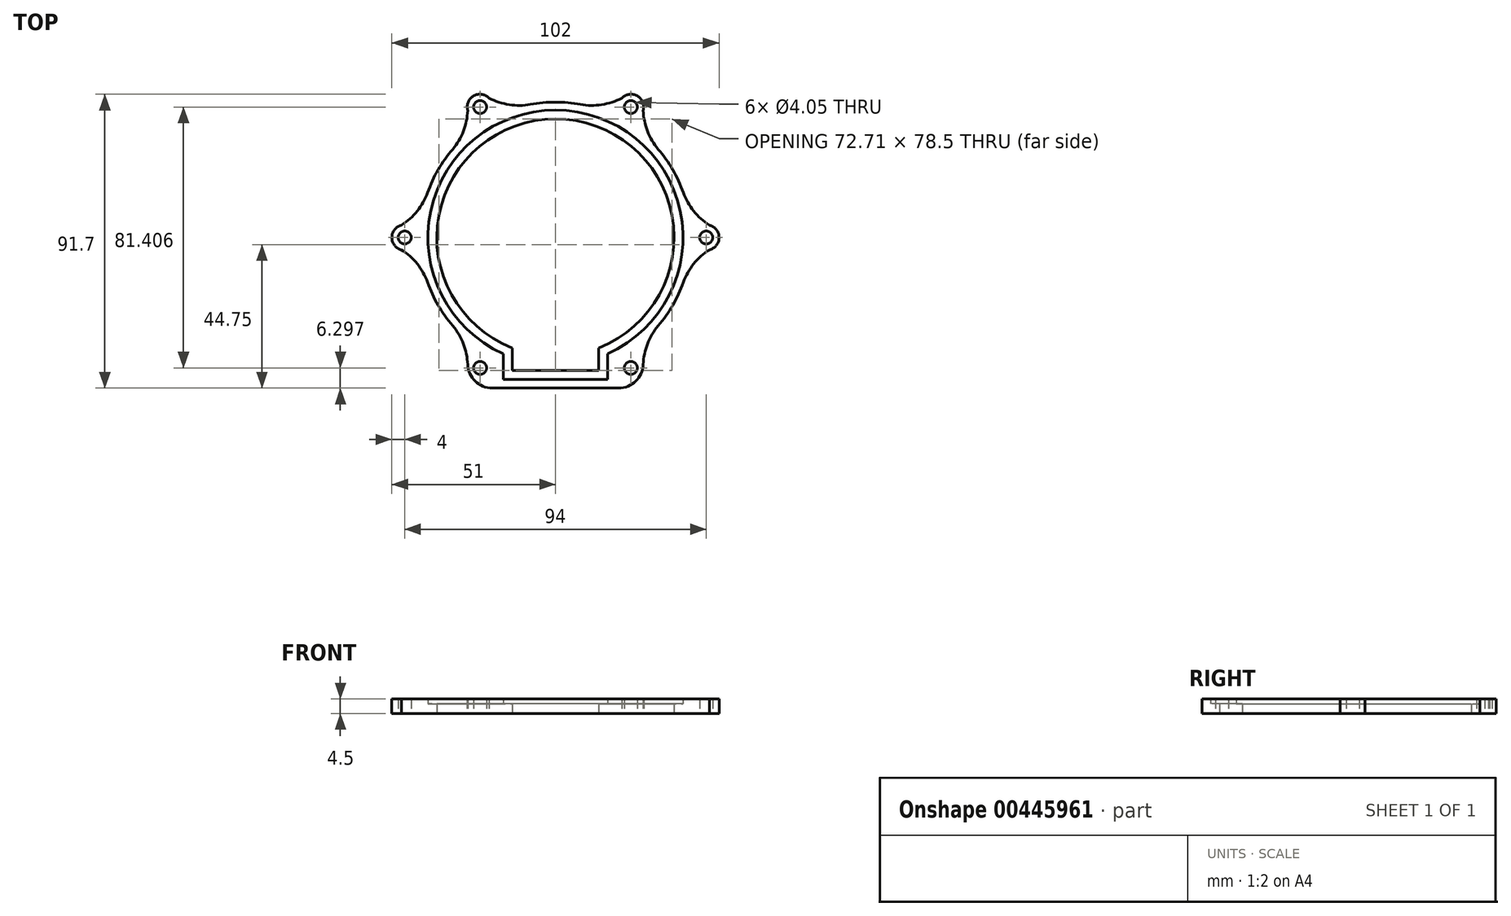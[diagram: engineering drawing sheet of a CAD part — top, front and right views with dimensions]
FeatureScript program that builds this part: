
annotation { "Feature Type Name" : "Feature", "Feature Type Description" : "" }
export const myFeature = defineFeature(function(context is Context, id is Id, definition is map)
    precondition{}
    {
        {
            var Q0;
            Q0=qCreatedBy(makeId("Top.planeOp"),FACE);
            var sketch = newSketch(context, id + "F0", { "sketchPlane" : qUnion([Q0])});
            skArc(sketch, "E0", {"start": v(13.5, -34.45) * mm, "mid": v(0, 37) * mm, "end": v(-13.5, -34.45) * mm});
            skArc(sketch, "E1", {"start": v(16.25, -36.28) * mm, "mid": v(0, 39.75) * mm, "end": v(-16.25, -36.28) * mm});
            skArc(sketch, "E2", {"start": v(-32.06, 27.52) * mm, "mid": v(-36.59, 21.12) * mm, "end": v(-39.86, 14) * mm});
            skArc(sketch, "E3", {"start": v(-48, 3.87) * mm, "mid": v(-51, 0) * mm, "end": v(-48, -3.87) * mm});
            skCircle(sketch, "E4", {"center": v(-47, 0) * mm, "radius": 2.02 * mm});
            skArc(sketch, "E5", {"start": v(-48, 3.87) * mm, "mid": v(-43.09, 8.26) * mm, "end": v(-39.86, 14) * mm});
            skArc(sketch, "E6.MirrorCS", {"start": v(-48, -3.87) * mm, "mid": v(-43.09, -8.26) * mm, "end": v(-39.86, -14) * mm});
            skArc(sketch, "E7.1.0", {"start": v(-27.35, -39.63) * mm, "mid": v(-28.7, -33.19) * mm, "end": v(-32.06, -27.52) * mm});
            skCircle(sketch, "E7.1.2", {"center": v(-23.5, -40.7) * mm, "radius": 2.02 * mm});
            skCircle(sketch, "E7.2.2", {"center": v(23.5, -40.7) * mm, "radius": 2.02 * mm});
            skArc(sketch, "E7.2.3", {"start": v(27.35, -39.63) * mm, "mid": v(28.7, -33.19) * mm, "end": v(32.06, -27.52) * mm});
            skArc(sketch, "E7.3.0", {"start": v(48, -3.87) * mm, "mid": v(43.09, -8.26) * mm, "end": v(39.86, -14) * mm});
            skArc(sketch, "E7.3.1", {"start": v(48, -3.87) * mm, "mid": v(51, 0) * mm, "end": v(48, 3.87) * mm});
            skCircle(sketch, "E7.3.2", {"center": v(47, 0) * mm, "radius": 2.02 * mm});
            skArc(sketch, "E7.3.3", {"start": v(48, 3.87) * mm, "mid": v(43.09, 8.26) * mm, "end": v(39.86, 14) * mm});
            skArc(sketch, "E7.4.0", {"start": v(27.35, 39.63) * mm, "mid": v(28.7, 33.19) * mm, "end": v(32.06, 27.52) * mm});
            skArc(sketch, "E7.4.1", {"start": v(27.35, 39.63) * mm, "mid": v(25.5, 44.17) * mm, "end": v(20.65, 43.5) * mm});
            skCircle(sketch, "E7.4.2", {"center": v(23.5, 40.7) * mm, "radius": 2.02 * mm});
            skArc(sketch, "E7.4.3", {"start": v(20.65, 43.5) * mm, "mid": v(14.4, 41.44) * mm, "end": v(7.8, 41.52) * mm});
            skArc(sketch, "E7.5.0", {"start": v(-20.65, 43.5) * mm, "mid": v(-14.4, 41.44) * mm, "end": v(-7.8, 41.52) * mm});
            skArc(sketch, "E7.5.1", {"start": v(-20.65, 43.5) * mm, "mid": v(-25.5, 44.17) * mm, "end": v(-27.35, 39.63) * mm});
            skCircle(sketch, "E7.5.2", {"center": v(-23.5, 40.7) * mm, "radius": 2.02 * mm});
            skArc(sketch, "E7.5.3", {"start": v(-27.35, 39.63) * mm, "mid": v(-28.7, 33.19) * mm, "end": v(-32.06, 27.52) * mm});
            skArc(sketch, "E8.trimOffspring", {"start": v(7.8, 41.52) * mm, "mid": v(0, 42.25) * mm, "end": v(-7.8, 41.52) * mm});
            skArc(sketch, "E9.trimOffspring", {"start": v(39.86, 14) * mm, "mid": v(36.59, 21.12) * mm, "end": v(32.06, 27.52) * mm});
            skArc(sketch, "E10.trimOffspring", {"start": v(32.06, -27.52) * mm, "mid": v(36.59, -21.13) * mm, "end": v(39.86, -14) * mm});
            skArc(sketch, "E11.trimOffspring", {"start": v(-39.86, -14) * mm, "mid": v(-36.59, -21.12) * mm, "end": v(-32.06, -27.52) * mm});
            skLineSegment(sketch, "E12.top", {"start": v(16.25, -44.25) * mm, "end": v(-16.25, -44.25) * mm});
            skLineSegment(sketch, "E12.left", {"start": v(16.25, -33.18) * mm, "end": v(16.25, -33.24) * mm});
            skLineSegment(sketch, "E12.right", {"start": v(-16.25, -33.18) * mm, "end": v(-16.25, -33.24) * mm});
            skPoint(sketch, "E12.middle", {"position": v(0, -38.72) * mm});
            skLineSegment(sketch, "E13.0", {"start": v(-13.5, -34.45) * mm, "end": v(-13.5, -41.5) * mm});
            skLineSegment(sketch, "E13.1", {"start": v(13.5, -41.5) * mm, "end": v(-13.5, -41.5) * mm});
            skLineSegment(sketch, "E13.2", {"start": v(13.5, -34.45) * mm, "end": v(13.5, -41.5) * mm});
            skLineSegment(sketch, "E14.1", {"start": v(19.69, -47) * mm, "end": v(-19.69, -47) * mm});
            skArc(sketch, "E15.trimOffspring", {"start": v(7.93, -41.5) * mm, "mid": v(7.87, -41.51) * mm, "end": v(7.8, -41.52) * mm});
            skArc(sketch, "E16.trimOffspring", {"start": v(-7.93, -41.5) * mm, "mid": v(-7.87, -41.51) * mm, "end": v(-7.8, -41.52) * mm});
            skLineSegment(sketch, "E17.trimOffspring", {"start": v(-16.25, -36.28) * mm, "end": v(-16.25, -44.25) * mm});
            skLineSegment(sketch, "E18.trimOffspring", {"start": v(16.25, -36.28) * mm, "end": v(16.25, -44.25) * mm});
            skArc(sketch, "E19", {"start": v(-27.35, -39.63) * mm, "mid": v(-25, -44.86) * mm, "end": v(-19.69, -47) * mm});
            skArc(sketch, "E20", {"start": v(27.35, -39.63) * mm, "mid": v(25, -44.86) * mm, "end": v(19.69, -47) * mm});
            skSolve(sketch);
        }
        {
            var Q0;
            Q0=makeQuery(id+"F0.imprint","IMPRINT",FACE,{"disambiguationData":[TD([[makeQuery(id+"F0.imprint","IMPRINT",EDGE,{"derivedFrom":sQuery(id+"F0.wireOp",EDGE,"E0")}),-1.0]])]});
            extrude(context, id + "F1", {"entities" : qUnion([Q0]), "depth" : 3 * mm});
        }
        {
            var Q0;
            Q0=makeQuery(id+"F0.imprint","IMPRINT",FACE,{"disambiguationData":[TD([[makeQuery(id+"F0.imprint","IMPRINT",EDGE,{"derivedFrom":sQuery(id+"F0.wireOp",EDGE,"E1")}),-1.0]])]});
            extrude(context, id + "F2", {"entities" : qUnion([Q0]), "operationType" : NewBodyOperationType.ADD, "depth" : 4.5 * mm});
        }
    });
